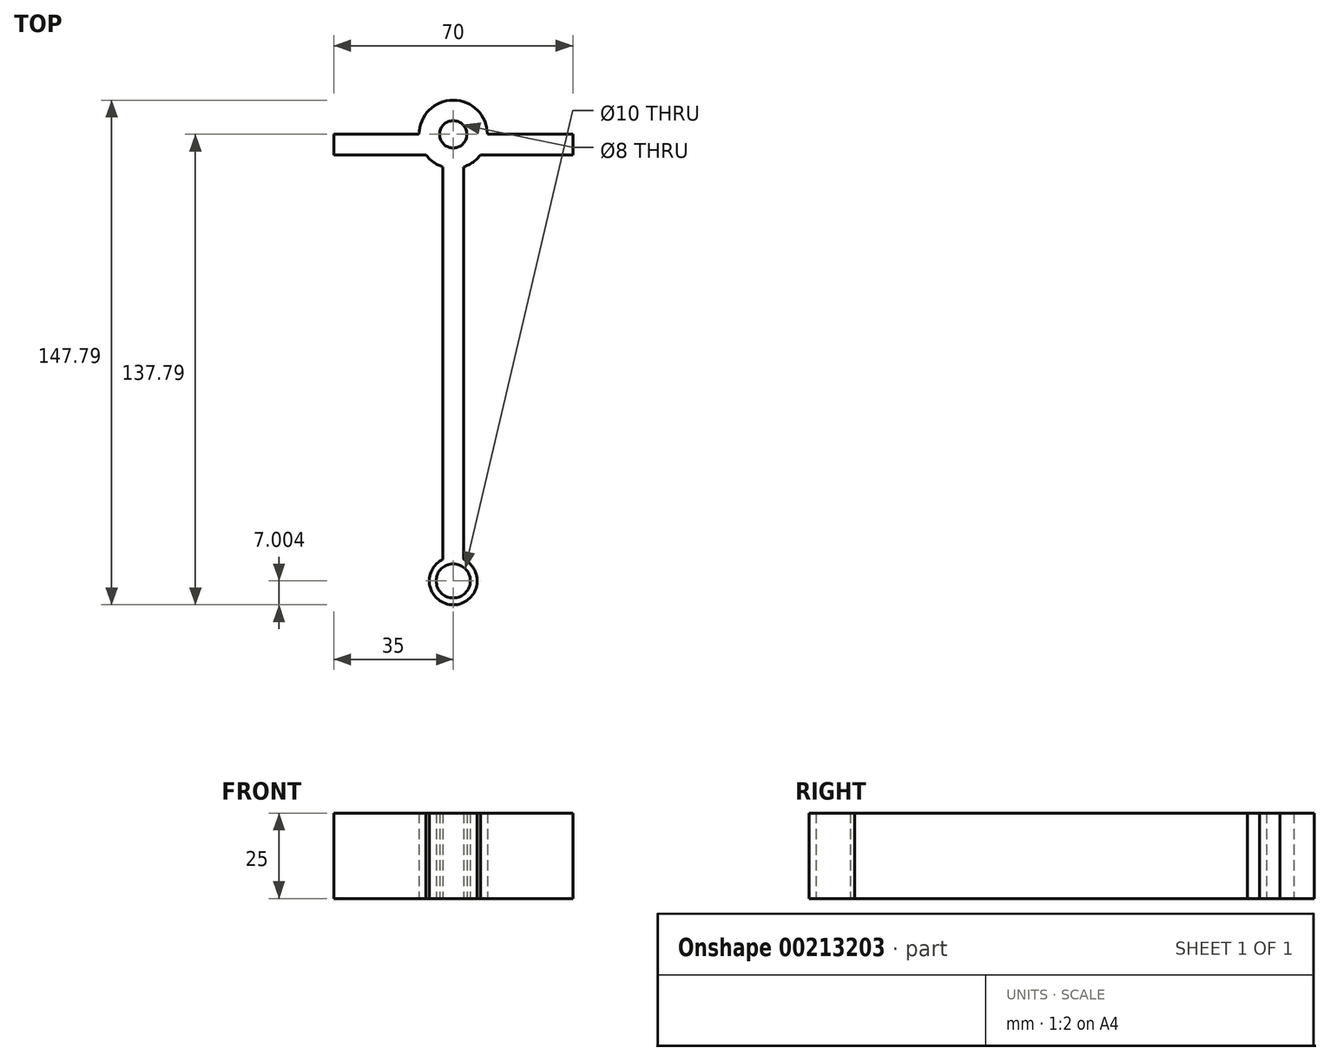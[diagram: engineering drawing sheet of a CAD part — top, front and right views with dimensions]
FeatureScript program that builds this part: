
annotation { "Feature Type Name" : "Feature", "Feature Type Description" : "" }
export const myFeature = defineFeature(function(context is Context, id is Id, definition is map)
    precondition{}
    {
        {
            var Q0;
            Q0=qCreatedBy(makeId("Top.planeOp"),FACE);
            var sketch = newSketch(context, id + "F0", { "sketchPlane" : qUnion([Q0])});
            skCircle(sketch, "E0", {"center": v(0, 0) * mm, "radius": 4 * mm});
            skCircle(sketch, "E1", {"center": v(0, 0) * mm, "radius": 10 * mm});
            skCircle(sketch, "E2", {"center": v(0, -130.79) * mm, "radius": 5 * mm});
            skCircle(sketch, "E3", {"center": v(0, -130.79) * mm, "radius": 7 * mm});
            skLineSegment(sketch, "E4.bottom", {"start": v(-3, -130.79) * mm, "end": v(3, -130.79) * mm});
            skLineSegment(sketch, "E4.top", {"start": v(-3, 0) * mm, "end": v(3, 0) * mm});
            skLineSegment(sketch, "E4.left", {"start": v(-3, -130.79) * mm, "end": v(-3, 0) * mm});
            skLineSegment(sketch, "E4.right", {"start": v(3, -130.79) * mm, "end": v(3, 0) * mm});
            skSolve(sketch);
        }
        {
            var Q0;
            {var subQ0=sQuery(id+"F0.wireOp",EDGE,"E4.left");var subQ1=sQuery(id+"F0.wireOp",EDGE,"E2");var subQ2=makeQuery(id+"F0.imprint","INTERSECT",VERTEX,{"derivedFrom":[subQ1,subQ0]});Q0=makeQuery(id+"F0.imprint","IMPRINT",FACE,{"disambiguationData":[TD([[makeQuery(id+"F0.imprint","IMPRINT",EDGE,{"disambiguationData":[TD([[subQ2,-1.0]])],"derivedFrom":subQ1}),-1.0]])]});}
            var Q1;
            {var subQ0=sQuery(id+"F0.wireOp",EDGE,"E4.left");var subQ1=sQuery(id+"F0.wireOp",EDGE,"E1");var subQ2=makeQuery(id+"F0.imprint","INTERSECT",VERTEX,{"derivedFrom":[subQ1,subQ0]});Q1=makeQuery(id+"F0.imprint","IMPRINT",FACE,{"disambiguationData":[TD([[makeQuery(id+"F0.imprint","IMPRINT",EDGE,{"disambiguationData":[TD([[subQ2,-1.0]])],"derivedFrom":subQ1}),-1.0]])]});}
            var Q2;
            {var subQ0=sQuery(id+"F0.wireOp",EDGE,"E4.left");var subQ1=sQuery(id+"F0.wireOp",EDGE,"E2");var subQ2=makeQuery(id+"F0.imprint","INTERSECT",VERTEX,{"derivedFrom":[subQ1,subQ0]});Q2=makeQuery(id+"F0.imprint","IMPRINT",FACE,{"disambiguationData":[TD([[makeQuery(id+"F0.imprint","IMPRINT",EDGE,{"disambiguationData":[TD([[subQ2,1.0]])],"derivedFrom":subQ1}),-1.0]])]});}
            var Q3;
            {var subQ0=sQuery(id+"F0.wireOp",EDGE,"E4.left");var subQ1=sQuery(id+"F0.wireOp",EDGE,"E0");var subQ2=makeQuery(id+"F0.imprint","INTERSECT",VERTEX,{"derivedFrom":[subQ1,subQ0]});Q3=makeQuery(id+"F0.imprint","IMPRINT",FACE,{"disambiguationData":[TD([[makeQuery(id+"F0.imprint","IMPRINT",EDGE,{"disambiguationData":[TD([[subQ2,1.0]])],"derivedFrom":subQ1}),-1.0]])]});}
            var Q4;
            {var subQ0=sQuery(id+"F0.wireOp",EDGE,"E4.left");var subQ1=sQuery(id+"F0.wireOp",EDGE,"E0");var subQ2=makeQuery(id+"F0.imprint","INTERSECT",VERTEX,{"derivedFrom":[subQ1,subQ0]});Q4=makeQuery(id+"F0.imprint","IMPRINT",FACE,{"disambiguationData":[TD([[makeQuery(id+"F0.imprint","IMPRINT",EDGE,{"disambiguationData":[TD([[subQ2,-1.0]])],"derivedFrom":subQ1}),-1.0]])]});}
            extrude(context, id + "F1", {"entities" : qUnion([Q0, Q1, Q2, Q3, Q4]), "depth" : 25 * mm});
        }
        {
            var Q0;
            Q0=qCreatedBy(makeId("Top.planeOp"),FACE);
            var sketch = newSketch(context, id + "F2", { "sketchPlane" : qUnion([Q0])});
            skLineSegment(sketch, "E5.bottom", {"start": v(-35, 0) * mm, "end": v(35, 0) * mm});
            skLineSegment(sketch, "E5.top", {"start": v(-35, -6) * mm, "end": v(35, -6) * mm});
            skLineSegment(sketch, "E5.left", {"start": v(-35, 0) * mm, "end": v(-35, -6) * mm});
            skLineSegment(sketch, "E5.right", {"start": v(35, 0) * mm, "end": v(35, -6) * mm});
            skCircle(sketch, "E6", {"center": v(0, 0) * mm, "radius": 4 * mm});
            skSolve(sketch);
        }
        {
            var Q0;
            {var subQ0=sQuery(id+"F2.wireOp",EDGE,"r1odGMaI-lZ1S-3sEL-j90L-70iIfEJ2N4Si");var subQ1=sQuery(id+"F2.wireOp",EDGE,"mmmAXoLk-yup9-Tajh-cjvy-FHtsMXsbCQbi");var subQ2=makeQuery(id+"F2.imprint","INTERSECT",VERTEX,{"disambiguationData":[OD(0.0)],"derivedFrom":[subQ1,subQ0]});Q0=makeQuery(id+"F2.imprint","IMPRINT",FACE,{"disambiguationData":[TD([[makeQuery(id+"F2.imprint","IMPRINT",EDGE,{"disambiguationData":[TD([[subQ2,-1.0]])],"derivedFrom":subQ1}),1.0]])]});}
            var Q1;
            Q1=makeQuery(id+"F2.imprint","IMPRINT",FACE,{"disambiguationData":[TD([[makeQuery(id+"F2.imprint","IMPRINT",EDGE,{"derivedFrom":sQuery(id+"F2.wireOp",EDGE,"E5.bottom")}),-1.0]])]});
            extrude(context, id + "F3", {"entities" : qUnion([Q0, Q1]), "operationType" : NewBodyOperationType.ADD, "depth" : 25 * mm});
        }
    });
